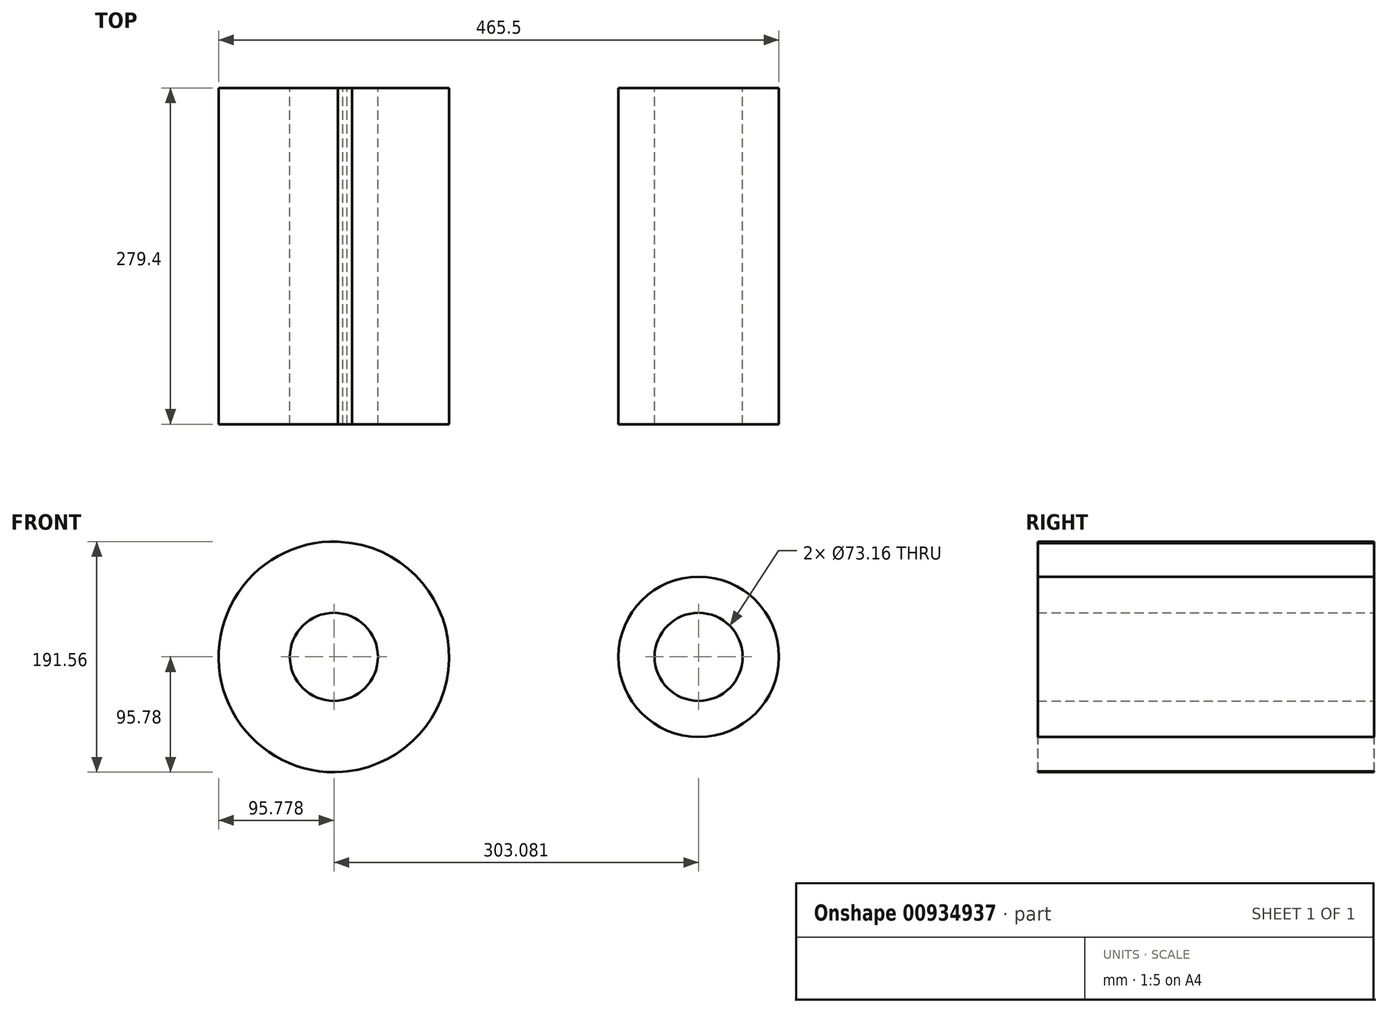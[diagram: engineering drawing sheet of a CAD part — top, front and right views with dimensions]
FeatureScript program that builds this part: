
annotation { "Feature Type Name" : "Feature", "Feature Type Description" : "" }
export const myFeature = defineFeature(function(context is Context, id is Id, definition is map)
    precondition{}
    {
        {
            var Q0;
            Q0=qCreatedBy(makeId("Front.planeOp"),FACE);
            var sketch = newSketch(context, id + "F0", { "sketchPlane" : qUnion([Q0])});
            skCircle(sketch, "E0", {"center": v(-167.21, 0) * mm, "radius": 95.78 * mm});
            skCircle(sketch, "E1", {"center": v(135.87, 0) * mm, "radius": 66.64 * mm});
            skCircle(sketch, "E2", {"center": v(-167.21, 0) * mm, "radius": 36.58 * mm});
            skCircle(sketch, "E3", {"center": v(135.87, 0) * mm, "radius": 36.58 * mm});
            skLineSegment(sketch, "E4", {"start": v(-163.93, 95.72) * mm, "end": v(142.24, 66.33) * mm});
            skLineSegment(sketch, "E5", {"start": v(-159.92, -95.5) * mm, "end": v(142.27, -66.33) * mm});
            skSolve(sketch);
        }
        {
            var Q0;
            {var subQ0=sQuery(id+"F0.wireOp",EDGE,"E4");var subQ1=sQuery(id+"F0.wireOp",EDGE,"E0");var subQ2=makeQuery(id+"F0.imprint","INTERSECT",VERTEX,{"disambiguationData":[OD(1.0)],"derivedFrom":[subQ1,subQ0]});Q0=makeQuery(id+"F0.imprint","IMPRINT",FACE,{"disambiguationData":[TD([[makeQuery(id+"F0.imprint","IMPRINT",EDGE,{"disambiguationData":[TD([[subQ2,1.0]])],"derivedFrom":subQ1}),-1.0]])]});}
            var Q1;
            Q1=makeQuery(id+"F0.imprint","IMPRINT",FACE,{"disambiguationData":[TD([[makeQuery(id+"F0.imprint","IMPRINT",EDGE,{"derivedFrom":sQuery(id+"F0.wireOp",EDGE,"E2")}),-1.0]])]});
            var Q2;
            Q2=makeQuery(id+"F0.imprint","IMPRINT",FACE,{"disambiguationData":[TD([[makeQuery(id+"F0.imprint","IMPRINT",EDGE,{"derivedFrom":sQuery(id+"F0.wireOp",EDGE,"E3")}),-1.0]])]});
            extrude(context, id + "F1", {"entities" : qUnion([Q0, Q1, Q2]), "depth" : 25.4 * mm, "offsetDistance" : 25.4 * mm, "hasSecondDirection" : true, "secondDirectionOppositeDirection" : true, "secondDirectionDepth" : 254 * mm});
        }
    });
